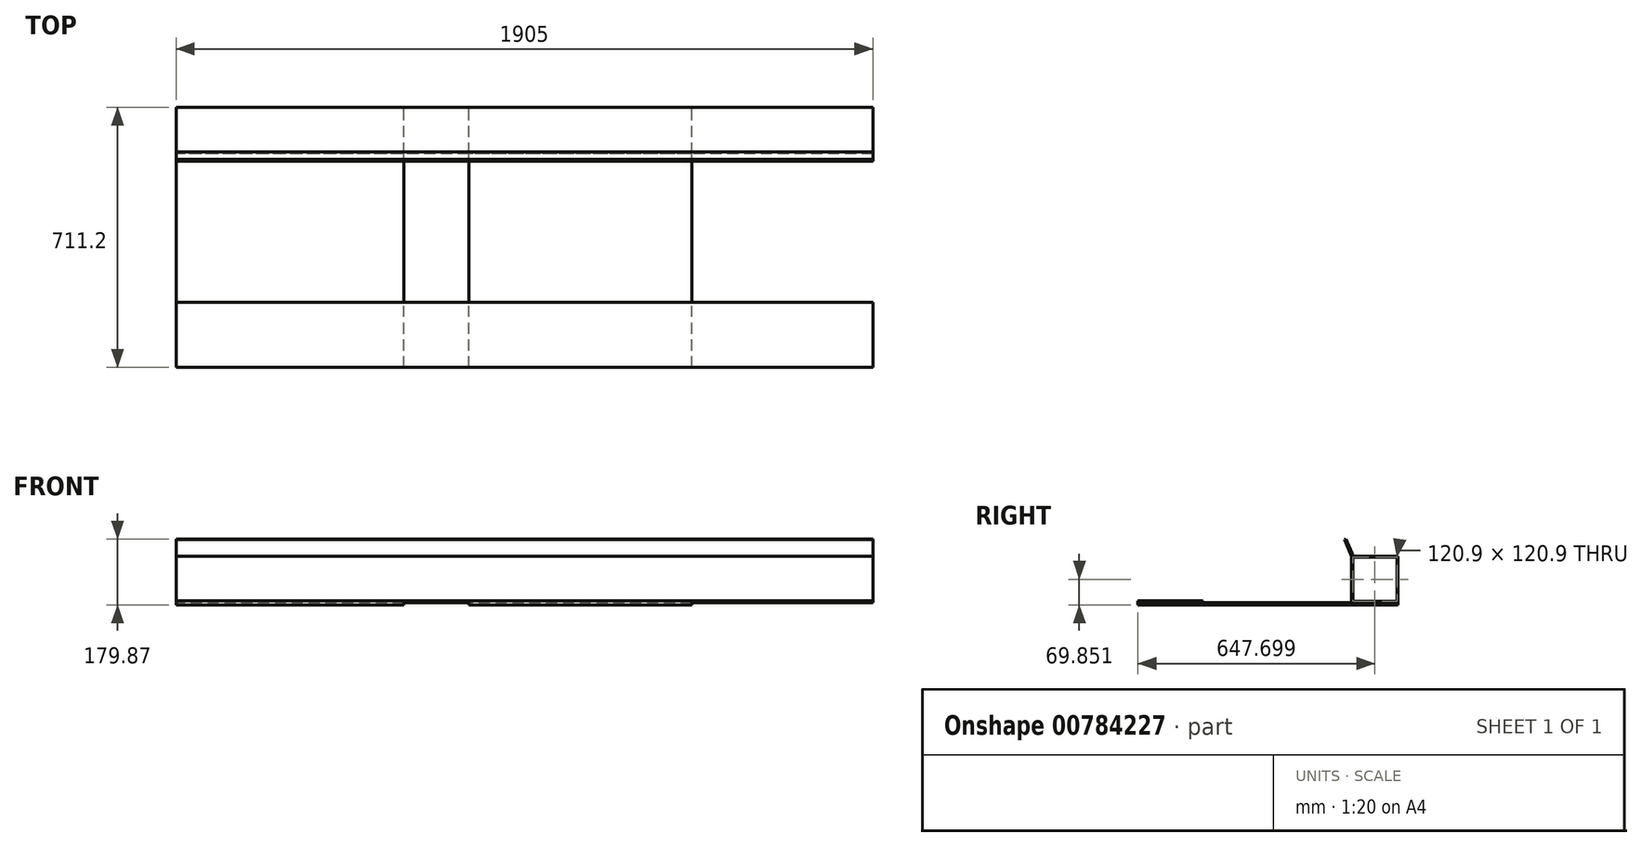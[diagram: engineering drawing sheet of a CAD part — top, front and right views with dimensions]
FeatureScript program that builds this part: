
annotation { "Feature Type Name" : "Feature", "Feature Type Description" : "" }
export const myFeature = defineFeature(function(context is Context, id is Id, definition is map)
    precondition{}
    {
        {
            var Q0;
            Q0=qCreatedBy(makeId("Right.planeOp"),FACE);
            var sketch = newSketch(context, id + "F0", { "sketchPlane" : qUnion([Q0])});
            skLineSegment(sketch, "E0.bottom", {"start": v(-58.57, 78.52) * mm, "end": v(68.43, 78.52) * mm});
            skLineSegment(sketch, "E0.top", {"start": v(-58.57, -48.48) * mm, "end": v(68.43, -48.48) * mm});
            skLineSegment(sketch, "E0.left", {"start": v(-58.57, 78.52) * mm, "end": v(-58.57, -48.48) * mm});
            skLineSegment(sketch, "E0.right", {"start": v(68.43, 78.52) * mm, "end": v(68.43, -48.48) * mm});
            skLineSegment(sketch, "E1.0", {"start": v(-55.52, 75.47) * mm, "end": v(65.38, 75.47) * mm});
            skLineSegment(sketch, "E1.1", {"start": v(-55.52, 75.47) * mm, "end": v(-55.52, -45.43) * mm});
            skLineSegment(sketch, "E1.2", {"start": v(-55.52, -45.43) * mm, "end": v(65.38, -45.43) * mm});
            skLineSegment(sketch, "E1.3", {"start": v(65.38, 75.47) * mm, "end": v(65.38, -45.43) * mm});
            skSolve(sketch);
        }
        {
            var Q0;
            Q0=makeQuery(id+"F0.imprint","IMPRINT",FACE,{"disambiguationData":[TD([[makeQuery(id+"F0.imprint","IMPRINT",EDGE,{"derivedFrom":sQuery(id+"F0.wireOp",EDGE,"E0.bottom")}),-1.0]])]});
            extrude(context, id + "F1", {"entities" : qUnion([Q0]), "depth" : 1905 * mm, "offsetDistance" : 25.4 * mm});
        }
        {
            var Q0;
            Q0=makeQuery(id+"F1.opExtrude","CAP_FACE",FACE,{"disambiguationData":[OSD([sQuery(id+"F0.wireOp",EDGE,"E0.bottom"),sQuery(id+"F0.wireOp",EDGE,"E0.top"),sQuery(id+"F0.wireOp",EDGE,"E0.left"),sQuery(id+"F0.wireOp",EDGE,"E0.right"),sQuery(id+"F0.wireOp",EDGE,"E1.0"),sQuery(id+"F0.wireOp",EDGE,"E1.1"),sQuery(id+"F0.wireOp",EDGE,"E1.2"),sQuery(id+"F0.wireOp",EDGE,"E1.3")])],"isStart":false});
            var sketch = newSketch(context, id + "F2", { "sketchPlane" : qUnion([Q0])});
            skLineSegment(sketch, "E2", {"start": v(-58.57, 78.52) * mm, "end": v(-78.51, 123.97) * mm});
            skLineSegment(sketch, "E3", {"start": v(-73.87, 125.04) * mm, "end": v(-53.46, 78.52) * mm});
            skLineSegment(sketch, "E4", {"start": v(-78.51, 123.97) * mm, "end": v(-73.87, 125.04) * mm});
            skSolve(sketch);
        }
        {
            var Q0;
            {var subQ0=sQuery(id+"F2.wireOp",EDGE,"E2");Q0=makeQuery(id+"F2.imprint","IMPRINT",FACE,{"disambiguationData":[TD([[makeQuery(id+"F2.imprint","IMPRINT",EDGE,{"derivedFrom":subQ0}),-1.0]])]});}
            extrude(context, id + "F3", {"entities" : qUnion([Q0]), "operationType" : NewBodyOperationType.ADD, "oppositeDirection" : true, "depth" : 1905 * mm, "offsetDistance" : 25.4 * mm});
        }
        {
            var Q0;
            Q0=makeQuery(id+"F1.opExtrude","SWEPT_FACE",FACE,{"disambiguationData":[OSD([sQuery(id+"F0.wireOp",EDGE,"E0.right")])]});
            var sketch = newSketch(context, id + "F4", { "sketchPlane" : qUnion([Q0])});
            skLineSegment(sketch, "E5.bottom", {"start": v(0, -48.48) * mm, "end": v(-1905, -48.48) * mm});
            skLineSegment(sketch, "E5.top", {"start": v(0, -54.83) * mm, "end": v(-1905, -54.83) * mm});
            skLineSegment(sketch, "E5.left", {"start": v(0, -48.48) * mm, "end": v(0, -54.83) * mm});
            skLineSegment(sketch, "E5.right", {"start": v(-1905, -48.48) * mm, "end": v(-1905, -54.83) * mm});
            skLineSegment(sketch, "E6", {"start": v(-622.3, -54.83) * mm, "end": v(-622.3, -48.48) * mm});
            skLineSegment(sketch, "E7", {"start": v(-800.1, -54.83) * mm, "end": v(-800.1, -48.48) * mm});
            skLineSegment(sketch, "E8", {"start": v(-1409.7, -54.83) * mm, "end": v(-1409.7, -48.48) * mm});
            skSolve(sketch);
        }
        {
            var Q0;
            {var subQ0=sQuery(id+"F4.wireOp",EDGE,"E5.left");Q0=makeQuery(id+"F4.imprint","IMPRINT",FACE,{"disambiguationData":[TD([[makeQuery(id+"F4.imprint","IMPRINT",EDGE,{"derivedFrom":subQ0}),-1.0]])]});}
            var Q1;
            {var subQ0=sQuery(id+"F4.wireOp",EDGE,"E7");Q1=makeQuery(id+"F4.imprint","IMPRINT",FACE,{"disambiguationData":[TD([[makeQuery(id+"F4.imprint","IMPRINT",EDGE,{"derivedFrom":subQ0}),1.0]])]});}
            extrude(context, id + "F5", {"entities" : qUnion([Q0, Q1]), "operationType" : NewBodyOperationType.ADD, "oppositeDirection" : true, "depth" : 711.2 * mm, "offsetDistance" : 25.4 * mm});
        }
        {
            var Q0;
            {var subQ0=sQuery(id+"F4.wireOp",EDGE,"E5.bottom");Q0=makeQuery(id+"F5.opExtrude","SWEPT_FACE",FACE,{"disambiguationData":[OSD([subQ0]),TDD([makeQuery(id+"F4.imprint","IMPRINT",EDGE,{"disambiguationData":[TD([[makeQuery(id+"F4.imprint","INTERSECT",VERTEX,{"derivedFrom":[subQ0,sQuery(id+"F4.wireOp",EDGE,"E6")]}),-1.0]])],"derivedFrom":subQ0})])]});}
            var sketch = newSketch(context, id + "F6", { "sketchPlane" : qUnion([Q0])});
            skLineSegment(sketch, "E9.bottom", {"start": v(0, -642.77) * mm, "end": v(1905, -642.77) * mm});
            skLineSegment(sketch, "E9.top", {"start": v(0, -464.97) * mm, "end": v(1905, -464.97) * mm});
            skLineSegment(sketch, "E9.left", {"start": v(0, -642.77) * mm, "end": v(0, -464.97) * mm});
            skLineSegment(sketch, "E9.right", {"start": v(1905, -642.77) * mm, "end": v(1905, -464.97) * mm});
            skSolve(sketch);
        }
        {
            var Q0;
            {var subQ5=sQuery(id+"F6.wireOp",EDGE,"E9.right");Q0=makeQuery(id+"F6.imprint","IMPRINT",FACE,{"disambiguationData":[TD([[makeQuery(id+"F6.imprint","IMPRINT",EDGE,{"derivedFrom":subQ5}),1.0]])]});}
            var Q1;
            {var subQ0=sQuery(id+"F6.wireOp",EDGE,"E9.left");Q1=makeQuery(id+"F6.imprint","IMPRINT",FACE,{"disambiguationData":[TD([[makeQuery(id+"F6.imprint","IMPRINT",EDGE,{"derivedFrom":subQ0}),-1.0]])]});}
            extrude(context, id + "F7", {"entities" : qUnion([Q0, Q1]), "operationType" : NewBodyOperationType.ADD, "depth" : 4.76 * mm, "offsetDistance" : 25.4 * mm});
        }
    });
